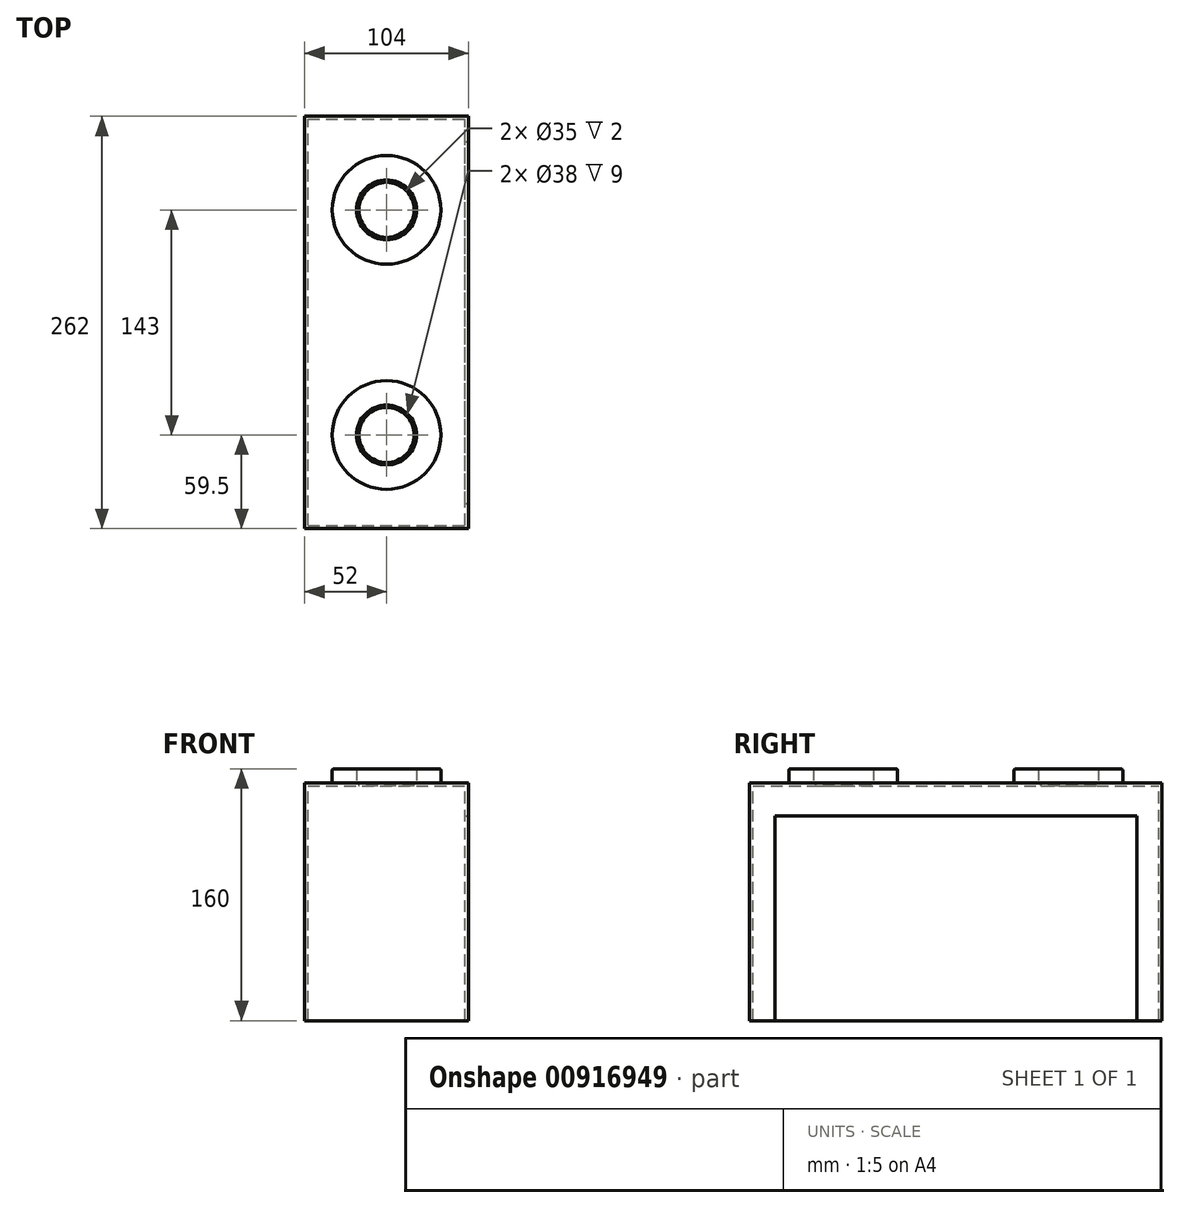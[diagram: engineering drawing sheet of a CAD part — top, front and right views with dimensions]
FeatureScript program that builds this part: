
annotation { "Feature Type Name" : "Feature", "Feature Type Description" : "" }
export const myFeature = defineFeature(function(context is Context, id is Id, definition is map)
    precondition{}
    {
        {
            var Q0;
            Q0=qCreatedBy(makeId("Front.planeOp"),FACE);
            var sketch = newSketch(context, id + "F0", { "sketchPlane" : qUnion([Q0])});
            skLineSegment(sketch, "E0.bottom", {"start": v(0, 0) * mm, "end": v(104, 0) * mm});
            skLineSegment(sketch, "E0.top", {"start": v(0, 151) * mm, "end": v(104, 151) * mm});
            skLineSegment(sketch, "E0.left", {"start": v(0, 0) * mm, "end": v(0, 151) * mm});
            skLineSegment(sketch, "E0.right", {"start": v(104, 0) * mm, "end": v(104, 151) * mm});
            skSolve(sketch);
        }
        {
            var Q0;
            Q0=makeQuery(id+"F0.imprint","IMPRINT",FACE,{"disambiguationData":[TD([[makeQuery(id+"F0.imprint","IMPRINT",EDGE,{"derivedFrom":sQuery(id+"F0.wireOp",EDGE,"E0.bottom")}),1.0]])]});
            extrude(context, id + "F1", {"entities" : qUnion([Q0]), "depth" : 262 * mm, "offsetDistance" : 25 * mm});
        }
        {
            var Q0;
            Q0=makeQuery(id+"F1.opExtrude","SWEPT_FACE",FACE,{"disambiguationData":[OSD([sQuery(id+"F0.wireOp",EDGE,"E0.bottom")])]});
            shell(context, id + "F2", {"entities" : qUnion([Q0]), "thickness" : 2 * mm});
        }
        {
            var Q0;
            Q0=makeQuery(id+"F1.opExtrude","SWEPT_FACE",FACE,{"disambiguationData":[OSD([sQuery(id+"F0.wireOp",EDGE,"E0.right")])]});
            var sketch = newSketch(context, id + "F3", { "sketchPlane" : qUnion([Q0])});
            skLineSegment(sketch, "E1.bottom", {"start": v(-246, 0) * mm, "end": v(-16, 0) * mm});
            skLineSegment(sketch, "E1.top", {"start": v(-246, 130) * mm, "end": v(-16, 130) * mm});
            skLineSegment(sketch, "E1.left", {"start": v(-246, 0) * mm, "end": v(-246, 130) * mm});
            skLineSegment(sketch, "E1.right", {"start": v(-16, 0) * mm, "end": v(-16, 130) * mm});
            skSolve(sketch);
        }
        {
            var Q0;
            Q0=makeQuery(id+"F3.imprint","IMPRINT",FACE,{"disambiguationData":[TD([[makeQuery(id+"F3.imprint","IMPRINT",EDGE,{"derivedFrom":sQuery(id+"F3.wireOp",EDGE,"E1.bottom")}),1.0]])]});
            extrude(context, id + "F4", {"entities" : qUnion([Q0]), "operationType" : NewBodyOperationType.REMOVE, "endBound" : BoundingType.UP_TO_NEXT, "oppositeDirection" : true, "depth" : 25 * mm, "offsetDistance" : 25 * mm});
        }
        {
            var Q0;
            Q0=makeQuery(id+"F1.opExtrude","SWEPT_FACE",FACE,{"disambiguationData":[OSD([sQuery(id+"F0.wireOp",EDGE,"E0.top")])]});
            var sketch = newSketch(context, id + "F5", { "sketchPlane" : qUnion([Q0])});
            skCircle(sketch, "E2", {"center": v(52, -59.5) * mm, "radius": 17.5 * mm});
            skPoint(sketch, "E2.centerSnap0", {"position": v(52, 0) * mm});
            skCircle(sketch, "E3", {"center": v(52, -202.5) * mm, "radius": 17.5 * mm});
            skSolve(sketch);
        }
        {
            var Q0;
            Q0=makeQuery(id+"F5.imprint","IMPRINT",FACE,{"disambiguationData":[TD([[makeQuery(id+"F5.imprint","IMPRINT",EDGE,{"derivedFrom":sQuery(id+"F5.wireOp",EDGE,"E2")}),1.0]])]});
            var Q1;
            Q1=makeQuery(id+"F5.imprint","IMPRINT",FACE,{"disambiguationData":[TD([[makeQuery(id+"F5.imprint","IMPRINT",EDGE,{"derivedFrom":sQuery(id+"F5.wireOp",EDGE,"E3")}),1.0]])]});
            extrude(context, id + "F6", {"entities" : qUnion([Q0, Q1]), "operationType" : NewBodyOperationType.REMOVE, "oppositeDirection" : true, "depth" : 25 * mm, "offsetDistance" : 25 * mm});
        }
        {
            var Q0;
            Q0=makeQuery(id+"F1.opExtrude","SWEPT_FACE",FACE,{"disambiguationData":[OSD([sQuery(id+"F0.wireOp",EDGE,"E0.top")])]});
            var sketch = newSketch(context, id + "F7", { "sketchPlane" : qUnion([Q0])});
            skCircle(sketch, "E4", {"center": v(52, -59.5) * mm, "radius": 34.5 * mm});
            skCircle(sketch, "E5", {"center": v(52, -59.5) * mm, "radius": 19 * mm});
            skCircle(sketch, "E6", {"center": v(52, -202.5) * mm, "radius": 19 * mm});
            skCircle(sketch, "E7", {"center": v(52, -202.5) * mm, "radius": 34.5 * mm});
            skSolve(sketch);
        }
        {
            var Q0;
            Q0=makeQuery(id+"F7.imprint","IMPRINT",FACE,{"disambiguationData":[TD([[makeQuery(id+"F7.imprint","IMPRINT",EDGE,{"derivedFrom":sQuery(id+"F7.wireOp",EDGE,"E4")}),1.0]])]});
            var Q1;
            Q1=makeQuery(id+"F7.imprint","IMPRINT",FACE,{"disambiguationData":[TD([[makeQuery(id+"F7.imprint","IMPRINT",EDGE,{"derivedFrom":sQuery(id+"F7.wireOp",EDGE,"E6")}),-1.0]])]});
            extrude(context, id + "F8", {"entities" : qUnion([Q0, Q1]), "operationType" : NewBodyOperationType.ADD, "depth" : 9 * mm, "offsetDistance" : 25 * mm});
        }
        {
            var Q0;
            Q0=makeQuery(id+"F8.opExtrude","CAP_EDGE",EDGE,{"disambiguationData":[OSD([sQuery(id+"F7.wireOp",EDGE,"E4")])],"isStart":false});
            var Q1;
            Q1=makeQuery(id+"F8.opExtrude","CAP_EDGE",EDGE,{"disambiguationData":[OSD([sQuery(id+"F7.wireOp",EDGE,"E7")])],"isStart":false});
            fillet(context, id + "F9", {"entities" : qUnion([Q0, Q1]), "radius" : 1 * mm, "tangentPropagation" : true, "allowEdgeOverflow" : false});
        }
    });
